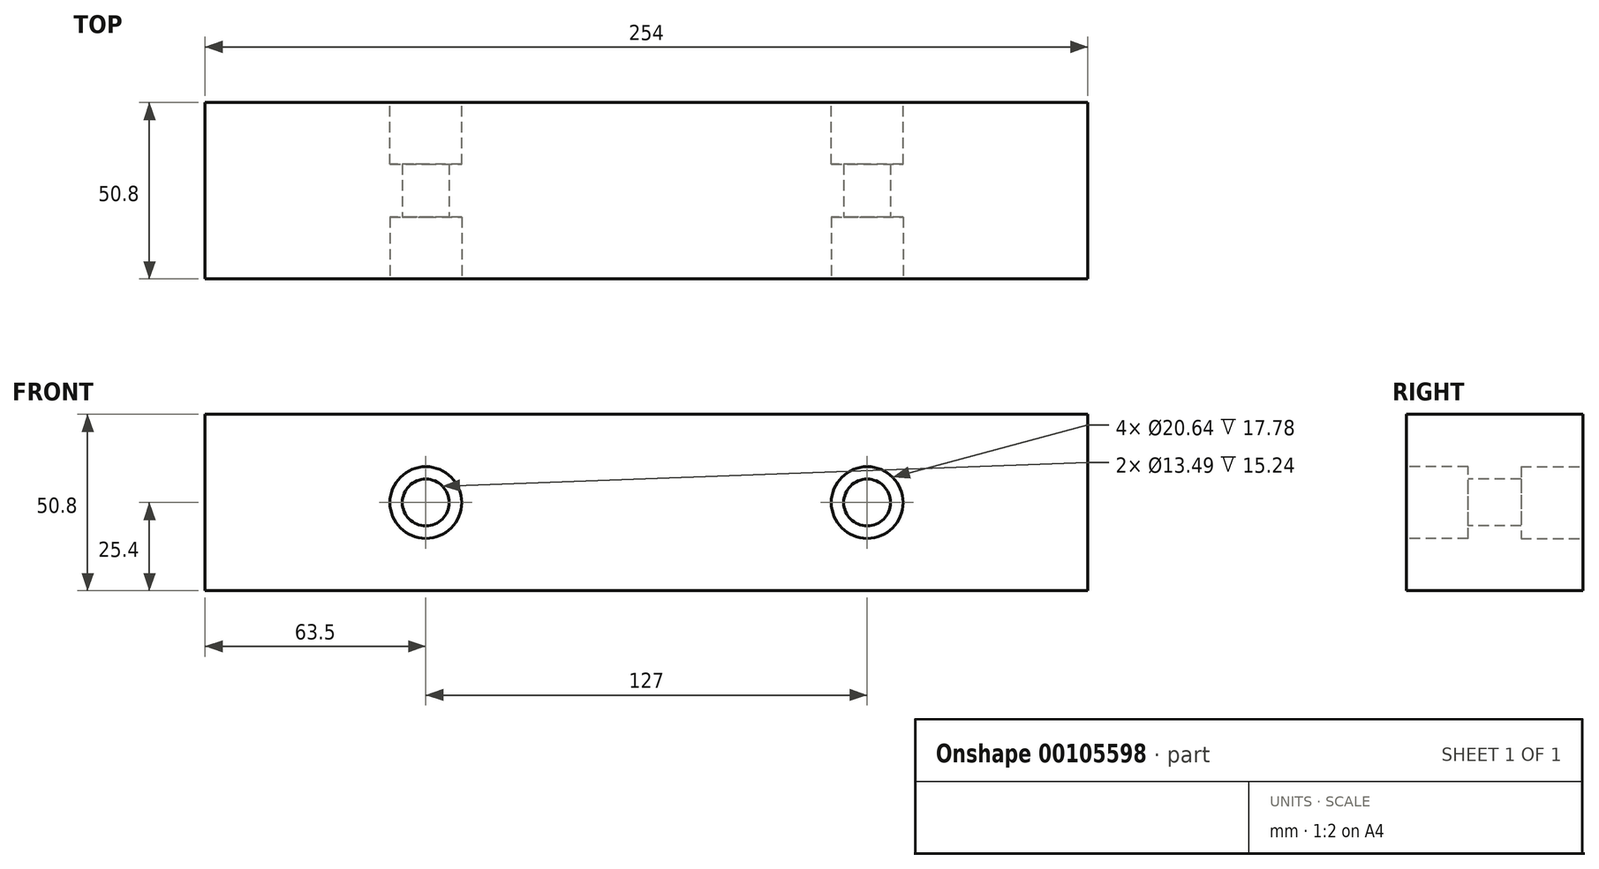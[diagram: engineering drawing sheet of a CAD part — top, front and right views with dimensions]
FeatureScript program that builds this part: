
annotation { "Feature Type Name" : "Feature", "Feature Type Description" : "" }
export const myFeature = defineFeature(function(context is Context, id is Id, definition is map)
    precondition{}
    {
        {
            var Q0;
            Q0=qCreatedBy(makeId("Front.planeOp"),FACE);
            var sketch = newSketch(context, id + "F0", { "sketchPlane" : qUnion([Q0])});
            skLineSegment(sketch, "E0.bottom", {"start": v(-127, 25.4) * mm, "end": v(127, 25.4) * mm});
            skLineSegment(sketch, "E0.top", {"start": v(-127, -25.4) * mm, "end": v(127, -25.4) * mm});
            skLineSegment(sketch, "E0.left", {"start": v(-127, 25.4) * mm, "end": v(-127, -25.4) * mm});
            skLineSegment(sketch, "E0.right", {"start": v(127, 25.4) * mm, "end": v(127, -25.4) * mm});
            skPoint(sketch, "E0.middle", {"position": v(0, 0) * mm});
            skSolve(sketch);
        }
        {
            var Q0;
            Q0=makeQuery(id+"F0.imprint","IMPRINT",FACE,{"disambiguationData":[TD([[makeQuery(id+"F0.imprint","IMPRINT",EDGE,{"derivedFrom":sQuery(id+"F0.wireOp",EDGE,"E0.bottom")}),-1.0]])]});
            extrude(context, id + "F1", {"entities" : qUnion([Q0]), "depth" : 50.8 * mm});
        }
        {
            var Q0;
            Q0=makeQuery(id+"F1.opExtrude","CAP_FACE",FACE,{"disambiguationData":[OSD([sQuery(id+"F0.wireOp",EDGE,"E0.bottom"),sQuery(id+"F0.wireOp",EDGE,"E0.top"),sQuery(id+"F0.wireOp",EDGE,"E0.left"),sQuery(id+"F0.wireOp",EDGE,"E0.right")])],"isStart":false});
            var sketch = newSketch(context, id + "F2", { "sketchPlane" : qUnion([Q0])});
            skPoint(sketch, "E1", {"position": v(-63.5, 0) * mm});
            skPoint(sketch, "E2", {"position": v(63.5, 0) * mm});
            skSolve(sketch);
        }
        {
            var Q0;
            Q0=sQuery(id+"F2.wireOp",VERTEX,"E1");
            var Q1;
            Q1=sQuery(id+"F2.wireOp",VERTEX,"E2");
            var Q2;
            Q2=makeQuery(id+"F1.opExtrude","SWEPT_BODY",BODY,{"disambiguationData":[OSD([sQuery(id+"F0.wireOp",EDGE,"E0.bottom"),sQuery(id+"F0.wireOp",EDGE,"E0.top"),sQuery(id+"F0.wireOp",EDGE,"E0.left"),sQuery(id+"F0.wireOp",EDGE,"E0.right")])]});
            hole(context, id + "F3", {"style" : HoleStyle.C_BORE, "endStyle" : HoleEndStyle.BLIND, "holeDiameter" : 13.5 * mm, "cBoreDiameter" : 20.64 * mm, "cBoreDepth" : 17.78 * mm, "holeDepth" : 25.4 * mm, "startFromSketch" : true, "locations" : qUnion([Q0, Q1]), "scope" : qUnion([Q2])});
        }
        {
            var Q0;
            Q0=makeQuery(id+"F1.opExtrude","CAP_FACE",FACE,{"disambiguationData":[OSD([sQuery(id+"F0.wireOp",EDGE,"E0.bottom"),sQuery(id+"F0.wireOp",EDGE,"E0.top"),sQuery(id+"F0.wireOp",EDGE,"E0.left"),sQuery(id+"F0.wireOp",EDGE,"E0.right")])],"isStart":true});
            var sketch = newSketch(context, id + "F4", { "sketchPlane" : qUnion([Q0])});
            skPoint(sketch, "E3", {"position": v(-63.5, 0) * mm});
            skPoint(sketch, "E4", {"position": v(63.5, 0) * mm});
            skSolve(sketch);
        }
        {
            var Q0;
            Q0=sQuery(id+"F4.wireOp",VERTEX,"E3");
            var Q1;
            Q1=sQuery(id+"F4.wireOp",VERTEX,"E4");
            var Q2;
            Q2=makeQuery(id+"F1.opExtrude","SWEPT_BODY",BODY,{"disambiguationData":[OSD([sQuery(id+"F0.wireOp",EDGE,"E0.bottom"),sQuery(id+"F0.wireOp",EDGE,"E0.top"),sQuery(id+"F0.wireOp",EDGE,"E0.left"),sQuery(id+"F0.wireOp",EDGE,"E0.right")])]});
            hole(context, id + "F5", {"style" : HoleStyle.C_BORE, "endStyle" : HoleEndStyle.BLIND, "holeDiameter" : 13.5 * mm, "cBoreDiameter" : 20.64 * mm, "cBoreDepth" : 17.78 * mm, "holeDepth" : 25.4 * mm, "startFromSketch" : true, "locations" : qUnion([Q0, Q1]), "scope" : qUnion([Q2])});
        }
    });
